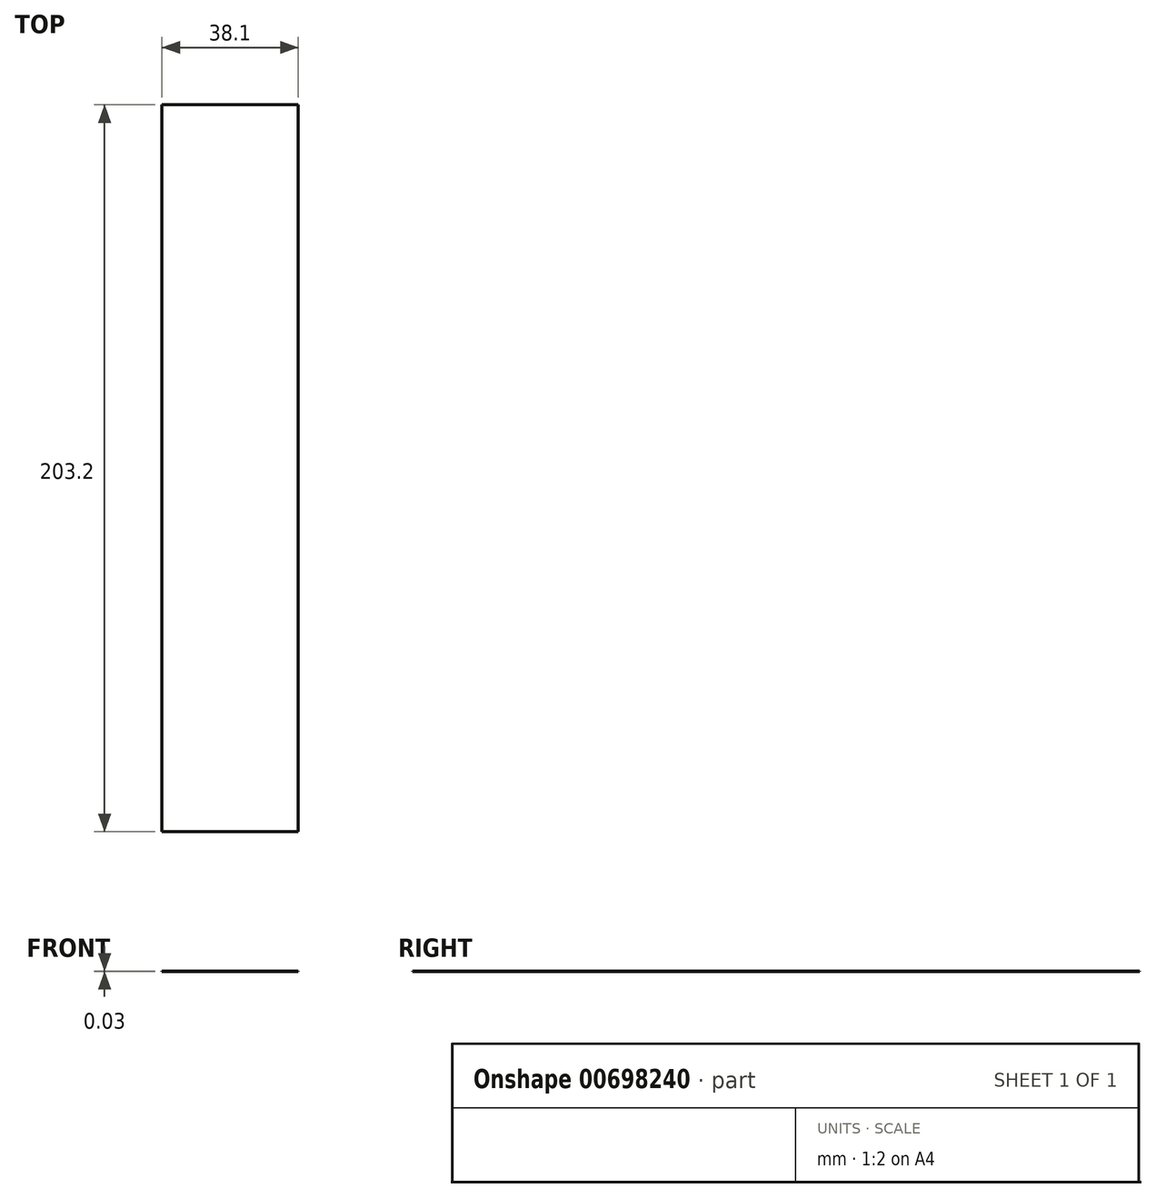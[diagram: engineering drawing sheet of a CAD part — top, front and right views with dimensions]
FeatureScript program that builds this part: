
annotation { "Feature Type Name" : "Feature", "Feature Type Description" : "" }
export const myFeature = defineFeature(function(context is Context, id is Id, definition is map)
    precondition{}
    {
        {
            var Q0;
            Q0=qCreatedBy(makeId("Top.planeOp"),FACE);
            var sketch = newSketch(context, id + "F0", { "sketchPlane" : qUnion([Q0])});
            skLineSegment(sketch, "E0.bottom", {"start": v(-33, 203.2) * mm, "end": v(5.1, 203.2) * mm});
            skLineSegment(sketch, "E0.top", {"start": v(-33, 0) * mm, "end": v(5.1, 0) * mm});
            skLineSegment(sketch, "E0.left", {"start": v(-33, 203.2) * mm, "end": v(-33, 0) * mm});
            skLineSegment(sketch, "E0.right", {"start": v(5.1, 203.2) * mm, "end": v(5.1, 0) * mm});
            skSolve(sketch);
        }
        {
            var Q0;
            Q0 = qSketchRegion(id + "F0", true);
            extrude(context, id + "F1", {"entities" : qUnion([Q0]), "depth" : 3 / 101.6 * mm, "offsetDistance" : 25.4 * mm});
        }
    });
